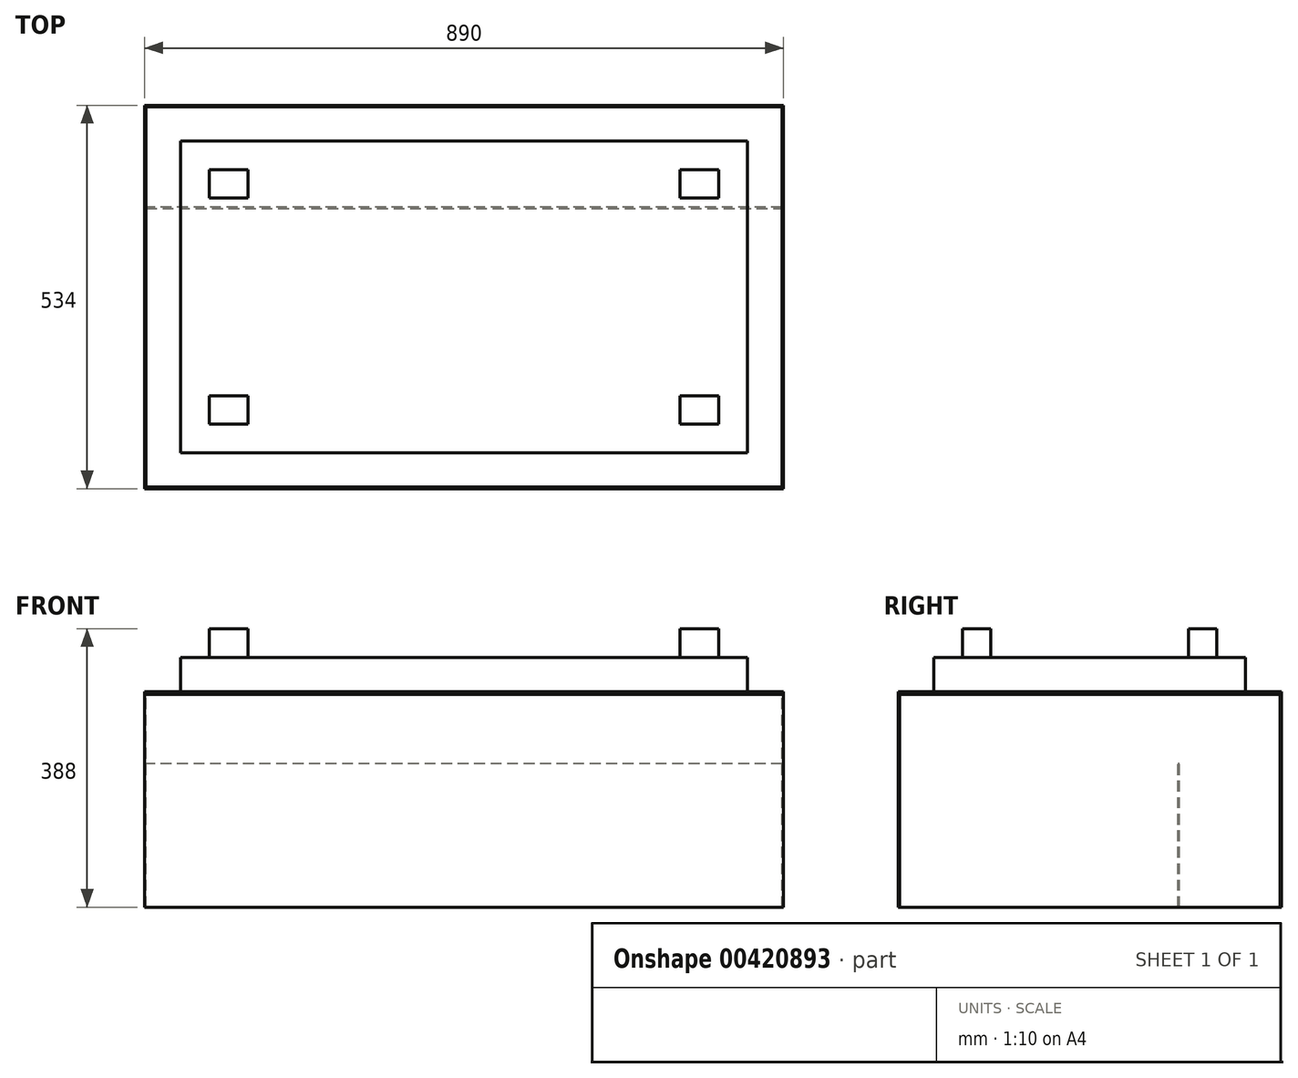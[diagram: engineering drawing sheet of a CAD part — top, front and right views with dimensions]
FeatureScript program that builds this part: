
annotation { "Feature Type Name" : "Feature", "Feature Type Description" : "" }
export const myFeature = defineFeature(function(context is Context, id is Id, definition is map)
    precondition{}
    {
        {
            var Q0;
            Q0=qCreatedBy(makeId("Top.planeOp"),FACE);
            var sketch = newSketch(context, id + "F0", { "sketchPlane" : qUnion([Q0])});
            skLineSegment(sketch, "E0.bottom", {"start": v(395, 217) * mm, "end": v(-395, 217) * mm});
            skLineSegment(sketch, "E0.top", {"start": v(395, -217) * mm, "end": v(-395, -217) * mm});
            skLineSegment(sketch, "E0.left", {"start": v(395, 217) * mm, "end": v(395, -217) * mm});
            skLineSegment(sketch, "E0.right", {"start": v(-395, 217) * mm, "end": v(-395, -217) * mm});
            skPoint(sketch, "E0.middle", {"position": v(0, 0) * mm});
            skSolve(sketch);
        }
        {
            var Q0;
            Q0=makeQuery(id+"F0.imprint","IMPRINT",FACE,{"disambiguationData":[TD([[makeQuery(id+"F0.imprint","IMPRINT",EDGE,{"derivedFrom":sQuery(id+"F0.wireOp",EDGE,"E0.bottom")}),1.0]])]});
            extrude(context, id + "F1", {"entities" : qUnion([Q0]), "oppositeDirection" : true, "depth" : 50 * mm});
        }
        {
            var Q0;
            Q0=makeQuery(id+"F1.opExtrude","CAP_FACE",FACE,{"disambiguationData":[OSD([sQuery(id+"F0.wireOp",EDGE,"E0.bottom"),sQuery(id+"F0.wireOp",EDGE,"E0.top"),sQuery(id+"F0.wireOp",EDGE,"E0.left"),sQuery(id+"F0.wireOp",EDGE,"E0.right")])],"isStart":false});
            var sketch = newSketch(context, id + "F2", { "sketchPlane" : qUnion([Q0])});
            skLineSegment(sketch, "E1.bottom", {"start": v(445, -267) * mm, "end": v(-445, -267) * mm});
            skLineSegment(sketch, "E1.top", {"start": v(445, 267) * mm, "end": v(-445, 267) * mm});
            skLineSegment(sketch, "E1.left", {"start": v(445, -267) * mm, "end": v(445, 267) * mm});
            skLineSegment(sketch, "E1.right", {"start": v(-445, -267) * mm, "end": v(-445, 267) * mm});
            skPoint(sketch, "E1.middle", {"position": v(0, 0) * mm});
            skSolve(sketch);
        }
        {
            var Q0;
            Q0 = qSketchRegion(id + "F2", true);
            extrude(context, id + "F3", {"entities" : qUnion([Q0]), "depth" : 2 * mm});
        }
        {
            var Q0;
            Q0=makeQuery(id+"F3.opExtrude","CAP_FACE",FACE,{"disambiguationData":[OSD([sQuery(id+"F2.wireOp",EDGE,"E1.bottom"),sQuery(id+"F2.wireOp",EDGE,"E1.top"),sQuery(id+"F2.wireOp",EDGE,"E1.left"),sQuery(id+"F2.wireOp",EDGE,"E1.right")])],"isStart":false});
            var sketch = newSketch(context, id + "F4", { "sketchPlane" : qUnion([Q0])});
            skLineSegment(sketch, "E2.bottom", {"start": v(-445, 267) * mm, "end": v(445, 267) * mm});
            skLineSegment(sketch, "E2.top", {"start": v(-445, 265) * mm, "end": v(445, 265) * mm});
            skLineSegment(sketch, "E2.left", {"start": v(-445, 267) * mm, "end": v(-445, 265) * mm});
            skLineSegment(sketch, "E2.right", {"start": v(445, 267) * mm, "end": v(445, 265) * mm});
            skSolve(sketch);
        }
        {
            var Q0;
            Q0 = qSketchRegion(id + "F4", true);
            extrude(context, id + "F5", {"entities" : qUnion([Q0]), "depth" : 300 * mm});
        }
        {
            var Q0;
            Q0=makeQuery(id+"F3.opExtrude","CAP_FACE",FACE,{"disambiguationData":[OSD([sQuery(id+"F2.wireOp",EDGE,"E1.bottom"),sQuery(id+"F2.wireOp",EDGE,"E1.top"),sQuery(id+"F2.wireOp",EDGE,"E1.left"),sQuery(id+"F2.wireOp",EDGE,"E1.right")])],"isStart":false});
            var sketch = newSketch(context, id + "F6", { "sketchPlane" : qUnion([Q0])});
            skLineSegment(sketch, "E3.bottom", {"start": v(-445, -267) * mm, "end": v(445, -267) * mm});
            skLineSegment(sketch, "E3.top", {"start": v(-445, -265) * mm, "end": v(445, -265) * mm});
            skLineSegment(sketch, "E3.left", {"start": v(-445, -267) * mm, "end": v(-445, -265) * mm});
            skLineSegment(sketch, "E3.right", {"start": v(445, -267) * mm, "end": v(445, -265) * mm});
            skSolve(sketch);
        }
        {
            var Q0;
            Q0 = qSketchRegion(id + "F6", true);
            extrude(context, id + "F7", {"entities" : qUnion([Q0]), "depth" : 300 * mm});
        }
        {
            var Q0;
            Q0=makeQuery(id+"F3.opExtrude","CAP_FACE",FACE,{"disambiguationData":[OSD([sQuery(id+"F2.wireOp",EDGE,"E1.bottom"),sQuery(id+"F2.wireOp",EDGE,"E1.top"),sQuery(id+"F2.wireOp",EDGE,"E1.left"),sQuery(id+"F2.wireOp",EDGE,"E1.right")])],"isStart":false});
            var sketch = newSketch(context, id + "F8", { "sketchPlane" : qUnion([Q0])});
            skLineSegment(sketch, "E4", {"start": v(-445, 264.97) * mm, "end": v(-443, 264.97) * mm});
            skLineSegment(sketch, "E5", {"start": v(-443, 264.97) * mm, "end": v(-443.27, -265.03) * mm});
            skLineSegment(sketch, "E6", {"start": v(-443.27, -265.03) * mm, "end": v(-445, -265.03) * mm});
            skLineSegment(sketch, "E7", {"start": v(-445, -265.03) * mm, "end": v(-445, 264.97) * mm});
            skLineSegment(sketch, "E8", {"start": v(0, 267) * mm, "end": v(0, -267) * mm, "construction": true});
            skLineSegment(sketch, "E9.MirrorCS", {"start": v(445, 264.97) * mm, "end": v(443, 264.97) * mm});
            skLineSegment(sketch, "E10.MirrorCS", {"start": v(445, -265.03) * mm, "end": v(445, 264.97) * mm});
            skLineSegment(sketch, "E11.MirrorCS", {"start": v(443, 264.97) * mm, "end": v(443.27, -265.03) * mm});
            skLineSegment(sketch, "E12.MirrorCS", {"start": v(443.27, -265.03) * mm, "end": v(445, -265.03) * mm});
            skSolve(sketch);
        }
        {
            var Q0;
            Q0 = qSketchRegion(id + "F8", true);
            extrude(context, id + "F9", {"entities" : qUnion([Q0]), "depth" : 300 * mm});
        }
        {
            var Q0;
            Q0=makeQuery(id+"F3.opExtrude","CAP_FACE",FACE,{"disambiguationData":[OSD([sQuery(id+"F2.wireOp",EDGE,"E1.bottom"),sQuery(id+"F2.wireOp",EDGE,"E1.top"),sQuery(id+"F2.wireOp",EDGE,"E1.left"),sQuery(id+"F2.wireOp",EDGE,"E1.right")])],"isStart":false});
            var sketch = newSketch(context, id + "F10", { "sketchPlane" : qUnion([Q0])});
            skLineSegment(sketch, "E13", {"start": v(-443, -125) * mm, "end": v(-443, -123) * mm});
            skLineSegment(sketch, "E14", {"start": v(-443, -123) * mm, "end": v(443.24, -123) * mm});
            skLineSegment(sketch, "E15", {"start": v(443.24, -123) * mm, "end": v(443.24, -125) * mm});
            skLineSegment(sketch, "E16", {"start": v(443.24, -125) * mm, "end": v(-443, -125) * mm});
            skSolve(sketch);
        }
        {
            var Q0;
            Q0 = qSketchRegion(id + "F10", true);
            extrude(context, id + "F11", {"entities" : qUnion([Q0]), "depth" : 200 * mm});
        }
        {
            var Q0;
            Q0=makeQuery(id+"F11.opExtrude","SWEPT_BODY",BODY,{"disambiguationData":[OSD([sQuery(id+"F10.wireOp",EDGE,"E13"),sQuery(id+"F10.wireOp",EDGE,"E14"),sQuery(id+"F10.wireOp",EDGE,"E15"),sQuery(id+"F10.wireOp",EDGE,"E16")])]});
            transform(context, id + "F12", {"entities" : qUnion([Q0]), "transformType" : TransformType.TRANSLATION_3D, "dx" : 0 * mm, "dy" : 0 * mm, "dz" : -96 * mm, "makeCopy" : false});
        }
        {
            var Q0;
            Q0=makeQuery(id+"F11.opExtrude","SWEPT_BODY",BODY,{"disambiguationData":[OSD([sQuery(id+"F10.wireOp",EDGE,"E13"),sQuery(id+"F10.wireOp",EDGE,"E14"),sQuery(id+"F10.wireOp",EDGE,"E15"),sQuery(id+"F10.wireOp",EDGE,"E16")])]});
            var Q1;
            Q1=makeQuery(id+"F3.opExtrude","SWEPT_BODY",BODY,{"disambiguationData":[OSD([sQuery(id+"F2.wireOp",EDGE,"E1.bottom"),sQuery(id+"F2.wireOp",EDGE,"E1.top"),sQuery(id+"F2.wireOp",EDGE,"E1.left"),sQuery(id+"F2.wireOp",EDGE,"E1.right")])]});
            var Q2;
            Q2=makeQuery(id+"F1.opExtrude","SWEPT_BODY",BODY,{"disambiguationData":[OSD([sQuery(id+"F0.wireOp",EDGE,"E0.bottom"),sQuery(id+"F0.wireOp",EDGE,"E0.top"),sQuery(id+"F0.wireOp",EDGE,"E0.left"),sQuery(id+"F0.wireOp",EDGE,"E0.right")])]});
            transform(context, id + "F13", {"entities" : qUnion([Q0, Q1, Q2]), "transformType" : TransformType.TRANSLATION_3D, "dx" : 0 * mm, "dy" : 0 * mm, "dz" : -4 * mm, "makeCopy" : false});
        }
        {
            var Q0;
            Q0=makeQuery(id+"F1.opExtrude","CAP_FACE",FACE,{"disambiguationData":[OSD([sQuery(id+"F0.wireOp",EDGE,"E0.bottom"),sQuery(id+"F0.wireOp",EDGE,"E0.top"),sQuery(id+"F0.wireOp",EDGE,"E0.left"),sQuery(id+"F0.wireOp",EDGE,"E0.right")])],"isStart":true});
            var sketch = newSketch(context, id + "F14", { "sketchPlane" : qUnion([Q0])});
            skLineSegment(sketch, "E17.bottom", {"start": v(-355, 177) * mm, "end": v(-301.15, 177) * mm});
            skLineSegment(sketch, "E17.top", {"start": v(-355, 137.63) * mm, "end": v(-301.15, 137.63) * mm});
            skLineSegment(sketch, "E17.left", {"start": v(-355, 177) * mm, "end": v(-355, 137.63) * mm});
            skLineSegment(sketch, "E17.right", {"start": v(-301.15, 177) * mm, "end": v(-301.15, 137.63) * mm});
            skLineSegment(sketch, "E18", {"start": v(0, 196.52) * mm, "end": v(0, -199.34) * mm, "construction": true});
            skLineSegment(sketch, "E19", {"start": v(-342.99, 0) * mm, "end": v(350.1, 0) * mm, "construction": true});
            skLineSegment(sketch, "E20.MirrorCS", {"start": v(355, 177) * mm, "end": v(301.15, 177) * mm});
            skLineSegment(sketch, "E21.MirrorCS", {"start": v(355, 177) * mm, "end": v(355, 137.63) * mm});
            skLineSegment(sketch, "E22.MirrorCS", {"start": v(355, 137.63) * mm, "end": v(301.15, 137.63) * mm});
            skLineSegment(sketch, "E23.MirrorCS", {"start": v(301.15, 177) * mm, "end": v(301.15, 137.63) * mm});
            skLineSegment(sketch, "E24.MirrorCS", {"start": v(-355, -177) * mm, "end": v(-301.15, -177) * mm});
            skLineSegment(sketch, "E25.MirrorCS", {"start": v(-355, -177) * mm, "end": v(-355, -137.63) * mm});
            skLineSegment(sketch, "E26.MirrorCS", {"start": v(-355, -137.63) * mm, "end": v(-301.15, -137.63) * mm});
            skLineSegment(sketch, "E27.MirrorCS", {"start": v(-301.15, -177) * mm, "end": v(-301.15, -137.63) * mm});
            skLineSegment(sketch, "E28.MirrorCS", {"start": v(355, -177) * mm, "end": v(301.15, -177) * mm});
            skLineSegment(sketch, "E29.MirrorCS", {"start": v(301.15, -177) * mm, "end": v(301.15, -137.63) * mm});
            skLineSegment(sketch, "E30.MirrorCS", {"start": v(355, -137.63) * mm, "end": v(301.15, -137.63) * mm});
            skLineSegment(sketch, "E31.MirrorCS", {"start": v(355, -177) * mm, "end": v(355, -137.63) * mm});
            skSolve(sketch);
        }
        {
            var Q0;
            Q0=makeQuery(id+"F14.imprint","IMPRINT",FACE,{"disambiguationData":[TD([[makeQuery(id+"F14.imprint","IMPRINT",EDGE,{"derivedFrom":sQuery(id+"F14.wireOp",EDGE,"E20.MirrorCS")}),1.0]])]});
            var Q1;
            Q1=makeQuery(id+"F14.imprint","IMPRINT",FACE,{"disambiguationData":[TD([[makeQuery(id+"F14.imprint","IMPRINT",EDGE,{"derivedFrom":sQuery(id+"F14.wireOp",EDGE,"E24.MirrorCS")}),1.0]])]});
            var Q2;
            Q2=makeQuery(id+"F14.imprint","IMPRINT",FACE,{"disambiguationData":[TD([[makeQuery(id+"F14.imprint","IMPRINT",EDGE,{"derivedFrom":sQuery(id+"F14.wireOp",EDGE,"E28.MirrorCS")}),-1.0]])]});
            var Q3;
            Q3=makeQuery(id+"F14.imprint","IMPRINT",FACE,{"disambiguationData":[TD([[makeQuery(id+"F14.imprint","IMPRINT",EDGE,{"derivedFrom":sQuery(id+"F14.wireOp",EDGE,"E17.bottom")}),-1.0]])]});
            extrude(context, id + "F15", {"entities" : qUnion([Q0, Q1, Q2, Q3]), "operationType" : NewBodyOperationType.ADD, "depth" : 40 * mm});
        }
        {
            var Q0;
            Q0=makeQuery(id+"F9.opExtrude","SWEPT_FACE",FACE,{"disambiguationData":[OSD([sQuery(id+"F8.wireOp",EDGE,"E10.MirrorCS")])]});
            var sketch = newSketch(context, id + "F16", { "sketchPlane" : qUnion([Q0])});
            skLineSegment(sketch, "E32", {"start": v(125, -73.7) * mm, "end": v(125, -352) * mm, "construction": true});
            skLineSegment(sketch, "E33", {"start": v(125, -352) * mm, "end": v(240.3, -256.43) * mm});
            skLineSegment(sketch, "E34", {"start": v(240.3, -256.43) * mm, "end": v(239.02, -254.9) * mm});
            skLineSegment(sketch, "E35", {"start": v(239.02, -254.9) * mm, "end": v(125, -349.4) * mm});
            skLineSegment(sketch, "E36", {"start": v(125, -349.4) * mm, "end": v(125, -352) * mm});
            skSolve(sketch);
        }
        {
            var Q0;
            {var subQ1=sQuery(id+"F16.wireOp",EDGE,"E33");Q0=makeQuery(id+"F16.imprint","IMPRINT",FACE,{"disambiguationData":[TD([[makeQuery(id+"F16.imprint","IMPRINT",EDGE,{"derivedFrom":subQ1}),-1.0]])]});}
            var Q1;
            Q1=sQuery(id+"F16.wireOp",EDGE,"E35");
            extrude(context, id + "F17", {"entities" : qUnion([Q0]), "bodyType" : ToolBodyType.SURFACE, "operationType" : NewBodyOperationType.INTERSECT, "surfaceEntities" : qUnion([Q1]), "oppositeDirection" : true, "depth" : 888 * mm});
        }
    });
